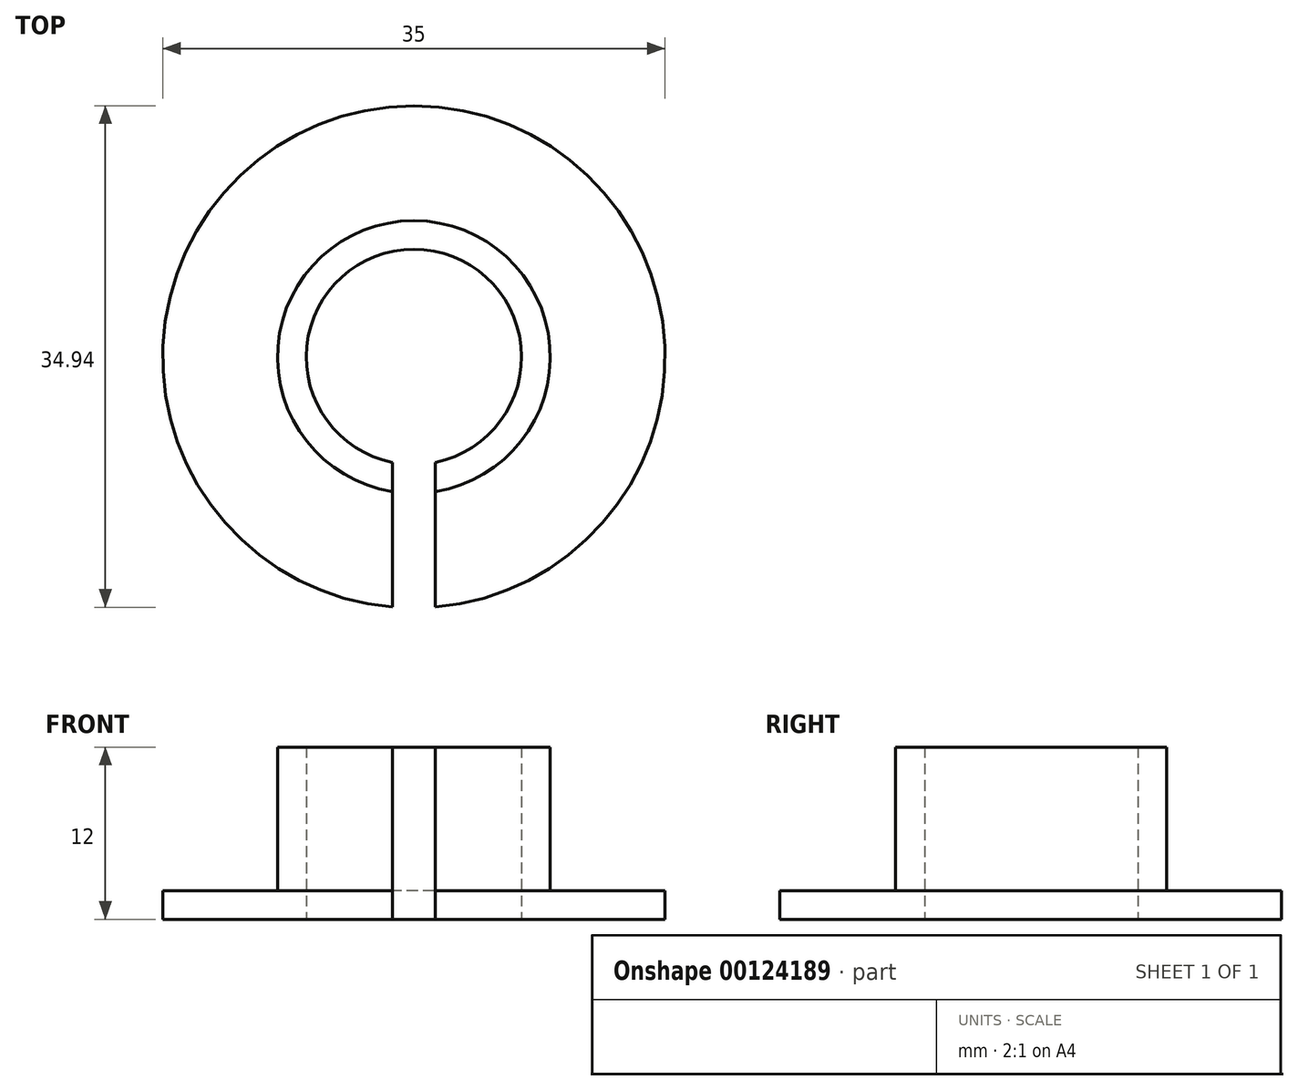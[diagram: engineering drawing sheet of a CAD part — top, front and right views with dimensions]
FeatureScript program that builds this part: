
annotation { "Feature Type Name" : "Feature", "Feature Type Description" : "" }
export const myFeature = defineFeature(function(context is Context, id is Id, definition is map)
    precondition{}
    {
        {
            var Q0;
            Q0=qCreatedBy(makeId("Top.planeOp"),FACE);
            var sketch = newSketch(context, id + "F0", { "sketchPlane" : qUnion([Q0])});
            skCircle(sketch, "E0", {"center": v(0, 0) * mm, "radius": 7.5 * mm});
            skCircle(sketch, "E1.0", {"center": v(0, 0) * mm, "radius": 17.5 * mm});
            skSolve(sketch);
        }
        {
            var Q0;
            Q0 = qSketchRegion(id + "F0", true);
            extrude(context, id + "F1", {"entities" : qUnion([Q0]), "depth" : 2 * mm});
        }
        {
            var Q0;
            Q0=makeQuery(id+"F1.opExtrude","CAP_FACE",FACE,{"disambiguationData":[OSD([sQuery(id+"F0.wireOp",EDGE,"E0"),sQuery(id+"F0.wireOp",EDGE,"E1.0")])],"isStart":false});
            var sketch = newSketch(context, id + "F2", { "sketchPlane" : qUnion([Q0])});
            skCircle(sketch, "E2.0", {"center": v(0, 0) * mm, "radius": 7.5 * mm});
            skCircle(sketch, "E3.0", {"center": v(0, 0) * mm, "radius": 9.5 * mm});
            skSolve(sketch);
        }
        {
            var Q0;
            Q0 = qSketchRegion(id + "F2", true);
            extrude(context, id + "F3", {"entities" : qUnion([Q0]), "operationType" : NewBodyOperationType.ADD, "depth" : 10 * mm});
        }
        {
            var Q0;
            Q0=qCreatedBy(makeId("Top.planeOp"),FACE);
            var sketch = newSketch(context, id + "F4", { "sketchPlane" : qUnion([Q0])});
            skLineSegment(sketch, "E4", {"start": v(0, 0) * mm, "end": v(0, -22.46) * mm, "construction": true});
            skLineSegment(sketch, "E5.bottom", {"start": v(-1.5, -17.5) * mm, "end": v(1.5, -17.5) * mm});
            skLineSegment(sketch, "E5.top", {"start": v(-1.5, -7.35) * mm, "end": v(1.5, -7.35) * mm});
            skLineSegment(sketch, "E5.left", {"start": v(-1.5, -17.5) * mm, "end": v(-1.5, -7.35) * mm});
            skLineSegment(sketch, "E5.right", {"start": v(1.5, -17.5) * mm, "end": v(1.5, -7.35) * mm});
            skPoint(sketch, "E5.middle", {"position": v(0, -12.42) * mm});
            skSolve(sketch);
        }
        {
            var Q0;
            Q0 = qSketchRegion(id + "F4", true);
            extrude(context, id + "F5", {"entities" : qUnion([Q0]), "operationType" : NewBodyOperationType.REMOVE, "endBound" : BoundingType.THROUGH_ALL, "depth" : 25 * mm});
        }
    });
